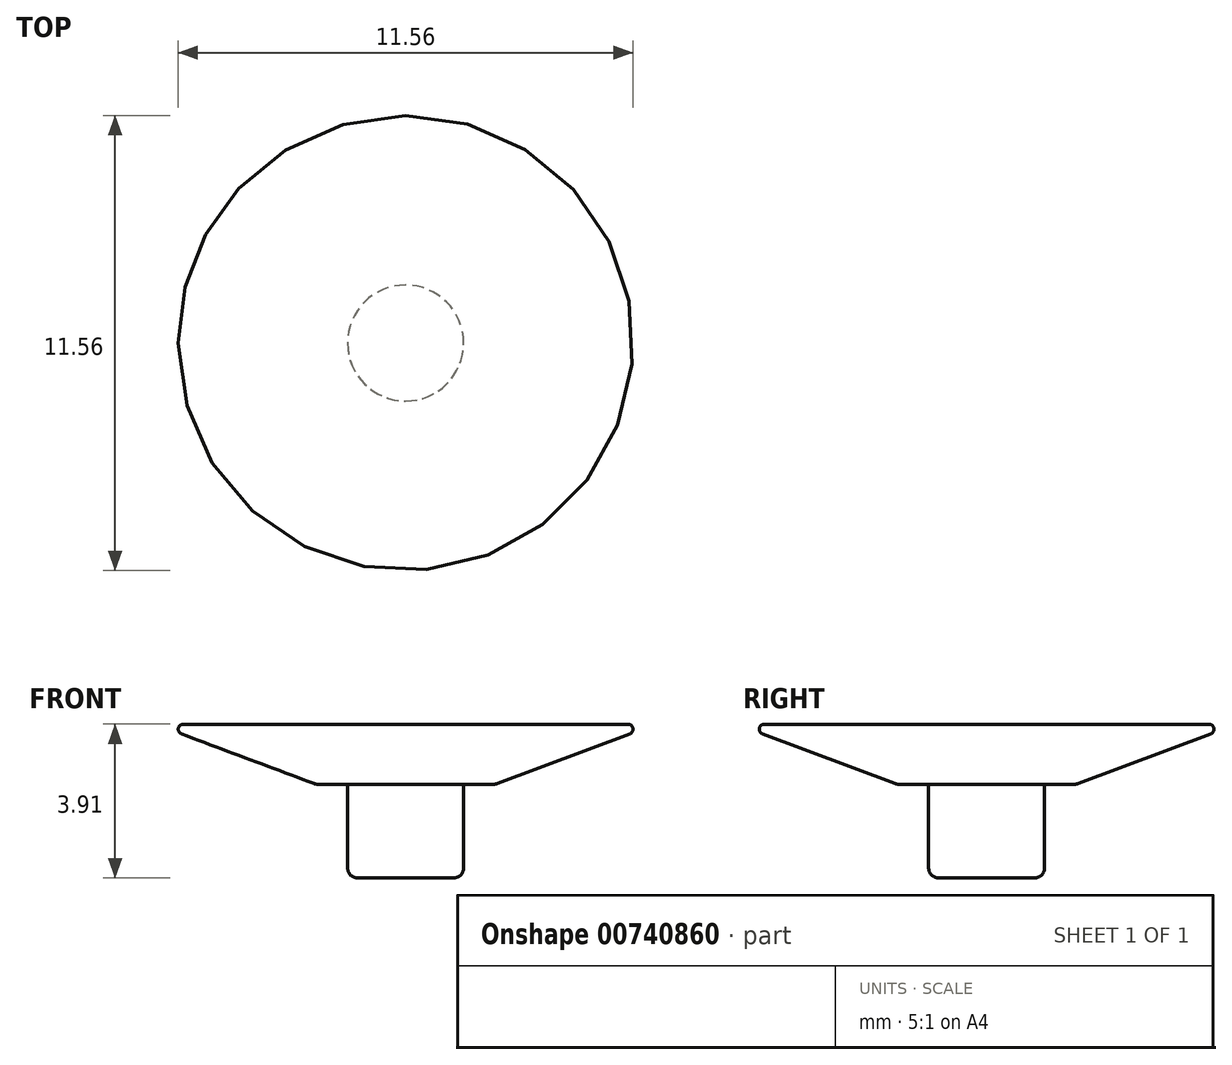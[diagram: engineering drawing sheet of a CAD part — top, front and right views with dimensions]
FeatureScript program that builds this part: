
annotation { "Feature Type Name" : "Feature", "Feature Type Description" : "" }
export const myFeature = defineFeature(function(context is Context, id is Id, definition is map)
    precondition{}
    {
        {
            var Q0;
            Q0=qCreatedBy(makeId("Front.planeOp"),FACE);
            var sketch = newSketch(context, id + "F0", { "sketchPlane" : qUnion([Q0])});
            skLineSegment(sketch, "E0", {"start": v(0, 0) * mm, "end": v(0, 3.9) * mm});
            skLineSegment(sketch, "E1", {"start": v(0, 3.9) * mm, "end": v(6.35, 3.9) * mm});
            skLineSegment(sketch, "E2", {"start": v(6.35, 3.9) * mm, "end": v(2.29, 2.38) * mm});
            skLineSegment(sketch, "E3", {"start": v(2.29, 2.38) * mm, "end": v(1.47, 2.38) * mm});
            skLineSegment(sketch, "E4", {"start": v(1.47, 2.38) * mm, "end": v(1.47, 0) * mm});
            skLineSegment(sketch, "E5", {"start": v(1.47, 0) * mm, "end": v(0, 0) * mm});
            skSolve(sketch);
        }
        {
            var Q0;
            Q0=makeQuery(id+"F0.imprint","IMPRINT",FACE,{"disambiguationData":[TD([[makeQuery(id+"F0.imprint","IMPRINT",EDGE,{"derivedFrom":sQuery(id+"F0.wireOp",EDGE,"E0")}),-1.0]])]});
            var Q1;
            Q1=sQuery(id+"F0.wireOp",EDGE,"E0");
            revolve(context, id + "F1", {"surfaceOperationType" : NewSurfaceOperationType.NEW, "entities" : qUnion([Q0]), "axis" : qUnion([Q1]), "revolveType" : RevolveType.FULL});
        }
        {
            var Q0;
            Q0=makeQuery(id+"F1.opRevolve","SWEPT_EDGE",EDGE,{"disambiguationData":[OSD([sQuery(id+"F0.wireOp",EDGE,"E2"),sQuery(id+"F0.wireOp",EDGE,"E3")])]});
            var Q1;
            Q1=makeQuery(id+"F1.opRevolve","SWEPT_EDGE",EDGE,{"disambiguationData":[OSD([sQuery(id+"F0.wireOp",EDGE,"E4"),sQuery(id+"F0.wireOp",EDGE,"E5")])]});
            fillet(context, id + "F2", {"entities" : qUnion([Q0, Q1]), "radius" : 0.25 * mm, "tangentPropagation" : true, "allowEdgeOverflow" : false});
        }
        {
            var Q0;
            Q0=makeQuery(id+"F1.opRevolve","SWEPT_EDGE",EDGE,{"disambiguationData":[OSD([sQuery(id+"F0.wireOp",EDGE,"E1"),sQuery(id+"F0.wireOp",EDGE,"E2")])]});
            fillet(context, id + "F3", {"entities" : qUnion([Q0]), "radius" : 0.13 * mm, "tangentPropagation" : true, "allowEdgeOverflow" : false});
        }
    });
